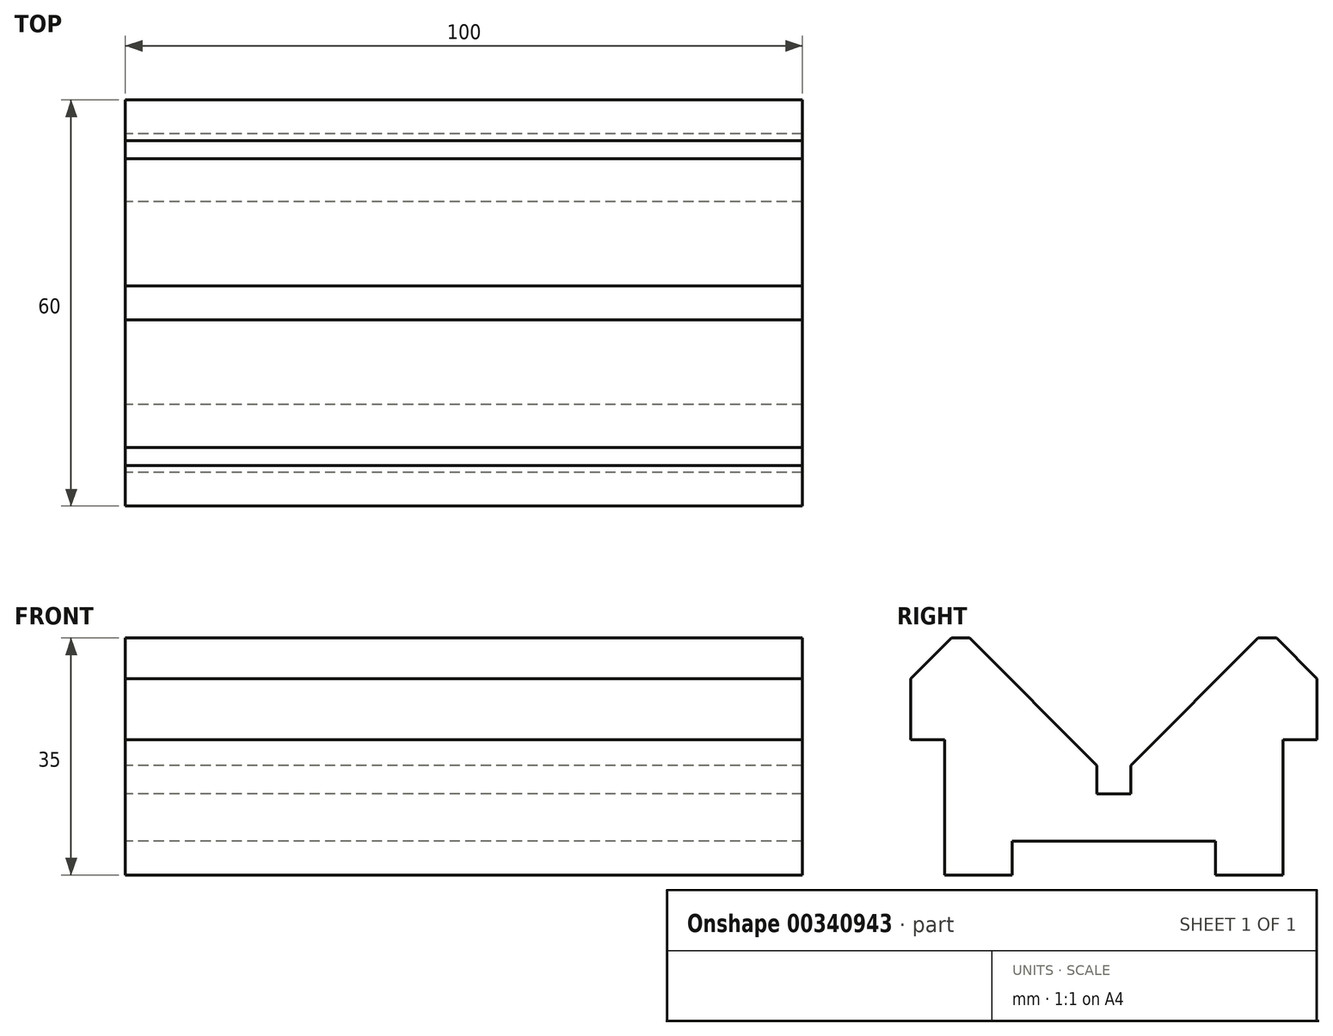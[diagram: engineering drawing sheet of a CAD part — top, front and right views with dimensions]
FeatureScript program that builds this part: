
annotation { "Feature Type Name" : "Feature", "Feature Type Description" : "" }
export const myFeature = defineFeature(function(context is Context, id is Id, definition is map)
    precondition{}
    {
        {
            var Q0;
            Q0=qCreatedBy(makeId("Right.planeOp"),FACE);
            var sketch = newSketch(context, id + "F0", { "sketchPlane" : qUnion([Q0])});
            skLineSegment(sketch, "E0", {"start": v(-18.5, -30) * mm, "end": v(-3.5, -30) * mm});
            skLineSegment(sketch, "E1", {"start": v(-3.5, -30) * mm, "end": v(-3.5, -35) * mm});
            skLineSegment(sketch, "E2", {"start": v(-3.5, -35) * mm, "end": v(6.5, -35) * mm});
            skLineSegment(sketch, "E3", {"start": v(6.5, -35) * mm, "end": v(6.5, -15) * mm});
            skLineSegment(sketch, "E4", {"start": v(6.5, -15) * mm, "end": v(11.5, -15) * mm});
            skLineSegment(sketch, "E5", {"start": v(11.5, -15) * mm, "end": v(11.5, -6) * mm});
            skLineSegment(sketch, "E6", {"start": v(11.5, -6) * mm, "end": v(5.5, 0) * mm});
            skLineSegment(sketch, "E7", {"start": v(5.5, 0) * mm, "end": v(2.81, 0) * mm});
            skLineSegment(sketch, "E8", {"start": v(2.81, 0) * mm, "end": v(-16, -18.82) * mm});
            skLineSegment(sketch, "E9", {"start": v(-16, -18.82) * mm, "end": v(-16, -23) * mm});
            skLineSegment(sketch, "E10", {"start": v(-18.5, -23) * mm, "end": v(-21, -23) * mm});
            skLineSegment(sketch, "E11", {"start": v(-21, -18.82) * mm, "end": v(-21, -23) * mm});
            skLineSegment(sketch, "E12", {"start": v(-16, -23) * mm, "end": v(-18.5, -23) * mm});
            skLineSegment(sketch, "E13", {"start": v(-18.5, -23) * mm, "end": v(-18.5, 8.55) * mm, "construction": true});
            skLineSegment(sketch, "E14", {"start": v(-18.5, -23) * mm, "end": v(-18.5, -37.06) * mm, "construction": true});
            skPoint(sketch, "E15.end.orphan", {"position": v(-48.5, -6) * mm});
            skPoint(sketch, "E16.start.orphan", {"position": v(-33.5, -30) * mm});
            skLineSegment(sketch, "E17.MirrorCS", {"start": v(-39.82, 0) * mm, "end": v(-21, -18.82) * mm});
            skLineSegment(sketch, "E18.MirrorCS", {"start": v(-33.5, -30) * mm, "end": v(-33.5, -35) * mm});
            skLineSegment(sketch, "E19.MirrorCS", {"start": v(-43.5, -15) * mm, "end": v(-48.5, -15) * mm});
            skLineSegment(sketch, "E20.MirrorCS", {"start": v(-48.5, -6) * mm, "end": v(-42.5, 0) * mm});
            skLineSegment(sketch, "E21.MirrorCS", {"start": v(-42.5, 0) * mm, "end": v(-39.82, 0) * mm});
            skLineSegment(sketch, "E22.MirrorCS", {"start": v(-33.5, -35) * mm, "end": v(-43.5, -35) * mm});
            skLineSegment(sketch, "E23.MirrorCS", {"start": v(-48.5, -15) * mm, "end": v(-48.5, -6) * mm});
            skLineSegment(sketch, "E24.MirrorCS", {"start": v(-43.5, -35) * mm, "end": v(-43.5, -15) * mm});
            skLineSegment(sketch, "E25.MirrorCS", {"start": v(-18.5, -30) * mm, "end": v(-33.5, -30) * mm});
            skSolve(sketch);
        }
        {
            var Q0;
            Q0 = qSketchRegion(id + "F0", true);
            extrude(context, id + "F1", {"entities" : qUnion([Q0]), "depth" : 100 * mm});
        }
    });
